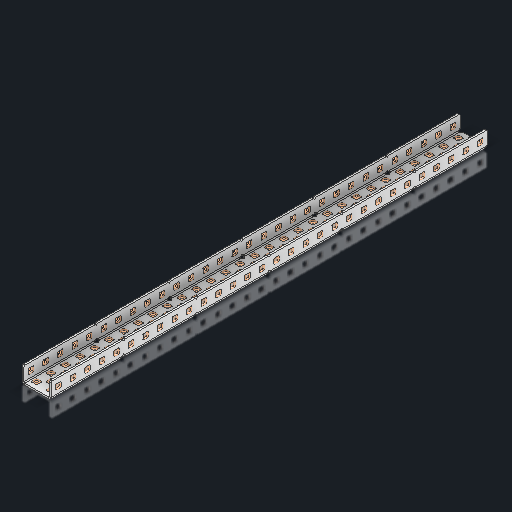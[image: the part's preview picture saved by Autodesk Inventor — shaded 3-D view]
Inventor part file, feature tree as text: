
AUTODESK INVENTOR PART (.ipt)
format: ipt  version: 2023.2 (Build 272271030, 271C)  size: 2,586,624 bytes
history: native  units: in
note: dims shown in document units (in); Inventor stores cm internally (conversion verified against a paired STEP export)
features: other x306, sketch x10, sheet_metal_op x1
ambient origin geometry x8: Origin, YZ Plane, XZ Plane, XY Plane, X Axis, Y Axis, Z Axis, Center Point
bodies: Solid1 (feature_tree)
feature tree (317):
  other  "Alu C 1x2x1x30_MIR.ipt"
  other  "Solid1::Alu C 1x2x1x30_MIR.ipt"
  other  "TaggingFeature1"
  sketch  "Sketch1"  dims[d0=0.3937in]
  sketch  "Sketch2"  dims[d1=0.0625in]
  sketch  "Sketch3"
  sketch  "Sketch7"
  other  "Flange Pattern Sketch"
  sketch  "Sketch8"
  sketch  "Sketch9"
  sheet_metal_op  "Body Pattern Sketch"
  sketch  "Sketch15"
  sketch  "Sketch16"
  other  "Arc Length"
  sketch  "Sketch13"
  sketch  "Sketch14"
  other  "Flange Pattern Plane"
  other  "Srf1"
  other  "Srf2"
  other  "Srf3"
  other  "Srf4"
  other  "Srf5"
  other  "Srf6"
  other  "Srf7"
  other  "Srf8"
  other  "Srf9"
  other  "Srf10"
  other  "Srf11"
  other  "Srf12"
  other  "Srf13"
  other  "Srf14"
  other  "Srf15"
  other  "Srf16"
  other  "Srf17"
  other  "Srf18"
  other  "Srf19"
  other  "Srf20"
  other  "Srf21"
  other  "Srf22"
  other  "Srf23"
  other  "Srf24"
  other  "Srf25"
  other  "Srf26"
  other  "Srf27"
  other  "Srf28"
  other  "Srf29"
  other  "Srf30"
  other  "Srf31"
  other  "Srf32"
  other  "Srf33"
  other  "Srf34"
  other  "Srf35"
  other  "Srf36"
  other  "Srf37"
  other  "Srf38"
  other  "Srf39"
  other  "Srf40"
  other  "Srf41"
  other  "Srf42"
  other  "Srf43"
  other  "Srf44"
  other  "Srf45"
  other  "Srf46"
  other  "Srf47"
  other  "Srf48"
  other  "Srf49"
  other  "Srf50"
  other  "Srf51"
  other  "Srf52"
  other  "Srf53"
  other  "Srf54"
  other  "Srf55"
  other  "Srf56"
  other  "Srf57"
  other  "Srf58"
  other  "Srf59"
  other  "Srf60"
  other  "Srf61"
  other  "Srf62"
  other  "Srf63"
  other  "Srf64"
  other  "Srf65"
  other  "Srf66"
  other  "Srf67"
  other  "Srf68"
  other  "Srf69"
  other  "Srf70"
  other  "Srf71"
  other  "Srf72"
  other  "Srf73"
  other  "Srf74"
  other  "Srf75"
  other  "Srf76"
  other  "Srf77"
  other  "Srf78"
  other  "Srf79"
  other  "Srf80"
  other  "Srf81"
  other  "Srf82"
  other  "Srf83"
  other  "Srf84"
  other  "Srf85"
  other  "Srf86"
  other  "Srf87"
  other  "Srf88"
  other  "Srf89"
  other  "Srf90"
  other  "Srf91"
  other  "Srf92"
  other  "Srf93"
  other  "Srf94"
  other  "Srf95"
  other  "Srf96"
  other  "Srf97"
  other  "Srf98"
  other  "Srf99"
  other  "Srf100"
  other  "Srf101"
  other  "Srf102"
  other  "Srf103"
  other  "Srf104"
  other  "Srf105"
  other  "Srf106"
  other  "Srf107"
  other  "Srf108"
  other  "Srf109"
  other  "Srf110"
  other  "Srf111"
  other  "Srf112"
  other  "Srf113"
  other  "Srf114"
  other  "Srf115"
  other  "Srf116"
  other  "Srf117"
  other  "Srf118"
  other  "Srf119"
  other  "Srf120"
  other  "Srf121"
  other  "Srf122"
  other  "Srf123"
  other  "Srf124"
  other  "Srf125"
  other  "Srf126"
  other  "Srf127"
  other  "Srf128"
  other  "Srf129"
  other  "Srf130"
  other  "Srf131"
  other  "Srf132"
  other  "Srf133"
  other  "Srf134"
  other  "Srf135"
  other  "Srf136"
  other  "Srf137"
  other  "Srf138"
  other  "Srf139"
  other  "Srf140"
  other  "Srf141"
  other  "Srf142"
  other  "Srf143"
  other  "Srf144"
  other  "Srf145"
  other  "Srf146"
  other  "Srf147"
  other  "Srf148"
  other  "Srf149"
  other  "Srf150"
  other  "Srf1::Derived"
  other  "Srf2::Derived"
  other  "Srf3::Derived"
  other  "Srf4::Derived"
  other  "Srf5::Derived"
  other  "Srf6::Derived"
  other  "Srf7::Derived"
  other  "Srf8::Derived"
  other  "Srf9::Derived"
  other  "Srf10::Derived"
  other  "Srf11::Derived"
  other  "Srf12::Derived"
  other  "Srf13::Derived"
  other  "Srf14::Derived"
  other  "Srf15::Derived"
  other  "Srf16::Derived"
  other  "Srf17::Derived"
  other  "Srf18::Derived"
  other  "Srf19::Derived"
  other  "Srf20::Derived"
  other  "Srf21::Derived"
  other  "Srf22::Derived"
  other  "Srf23::Derived"
  other  "Srf24::Derived"
  other  "Srf25::Derived"
  other  "Srf26::Derived"
  other  "Srf27::Derived"
  other  "Srf28::Derived"
  other  "Srf29::Derived"
  other  "Srf30::Derived"
  other  "Srf31::Derived"
  other  "Srf32::Derived"
  other  "Srf33::Derived"
  other  "Srf34::Derived"
  other  "Srf35::Derived"
  other  "Srf36::Derived"
  other  "Srf37::Derived"
  other  "Srf38::Derived"
  other  "Srf39::Derived"
  other  "Srf40::Derived"
  other  "Srf41::Derived"
  other  "Srf42::Derived"
  other  "Srf43::Derived"
  other  "Srf44::Derived"
  other  "Srf45::Derived"
  other  "Srf46::Derived"
  other  "Srf47::Derived"
  other  "Srf48::Derived"
  other  "Srf49::Derived"
  other  "Srf50::Derived"
  other  "Srf51::Derived"
  other  "Srf52::Derived"
  other  "Srf53::Derived"
  other  "Srf54::Derived"
  other  "Srf55::Derived"
  other  "Srf56::Derived"
  other  "Srf57::Derived"
  other  "Srf58::Derived"
  other  "Srf59::Derived"
  other  "Srf60::Derived"
  other  "Srf61::Derived"
  other  "Srf62::Derived"
  other  "Srf63::Derived"
  other  "Srf64::Derived"
  other  "Srf65::Derived"
  other  "Srf66::Derived"
  other  "Srf67::Derived"
  other  "Srf68::Derived"
  other  "Srf69::Derived"
  other  "Srf70::Derived"
  other  "Srf71::Derived"
  other  "Srf72::Derived"
  other  "Srf73::Derived"
  other  "Srf74::Derived"
  other  "Srf75::Derived"
  other  "Srf76::Derived"
  other  "Srf77::Derived"
  other  "Srf78::Derived"
  other  "Srf79::Derived"
  other  "Srf80::Derived"
  other  "Srf81::Derived"
  other  "Srf82::Derived"
  other  "Srf83::Derived"
  other  "Srf84::Derived"
  other  "Srf85::Derived"
  other  "Srf86::Derived"
  other  "Srf87::Derived"
  other  "Srf88::Derived"
  other  "Srf89::Derived"
  other  "Srf90::Derived"
  other  "Srf91::Derived"
  other  "Srf92::Derived"
  other  "Srf93::Derived"
  other  "Srf94::Derived"
  other  "Srf95::Derived"
  other  "Srf96::Derived"
  other  "Srf97::Derived"
  other  "Srf98::Derived"
  other  "Srf99::Derived"
  other  "Srf100::Derived"
  other  "Srf101::Derived"
  other  "Srf102::Derived"
  other  "Srf103::Derived"
  other  "Srf104::Derived"
  other  "Srf105::Derived"
  other  "Srf106::Derived"
  other  "Srf107::Derived"
  other  "Srf108::Derived"
  other  "Srf109::Derived"
  other  "Srf110::Derived"
  other  "Srf111::Derived"
  other  "Srf112::Derived"
  other  "Srf113::Derived"
  other  "Srf114::Derived"
  other  "Srf115::Derived"
  other  "Srf116::Derived"
  other  "Srf117::Derived"
  other  "Srf118::Derived"
  other  "Srf119::Derived"
  other  "Srf120::Derived"
  other  "Srf121::Derived"
  other  "Srf122::Derived"
  other  "Srf123::Derived"
  other  "Srf124::Derived"
  other  "Srf125::Derived"
  other  "Srf126::Derived"
  other  "Srf127::Derived"
  other  "Srf128::Derived"
  other  "Srf129::Derived"
  other  "Srf130::Derived"
  other  "Srf131::Derived"
  other  "Srf132::Derived"
  other  "Srf133::Derived"
  other  "Srf134::Derived"
  other  "Srf135::Derived"
  other  "Srf136::Derived"
  other  "Srf137::Derived"
  other  "Srf138::Derived"
  other  "Srf139::Derived"
  other  "Srf140::Derived"
  other  "Srf141::Derived"
  other  "Srf142::Derived"
  other  "Srf143::Derived"
  other  "Srf144::Derived"
  other  "Srf145::Derived"
  other  "Srf146::Derived"
  other  "Srf147::Derived"
  other  "Srf148::Derived"
  other  "Srf149::Derived"
  other  "Srf150::Derived"
